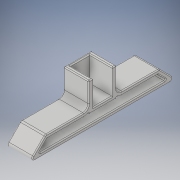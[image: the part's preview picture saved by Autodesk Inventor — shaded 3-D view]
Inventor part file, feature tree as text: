
AUTODESK INVENTOR PART (.ipt)
format: ipt  version: 2019 (Build 230136000, 136)  size: 265,728 bytes
history: native  units: in
note: dims shown in document units (in); Inventor stores cm internally (conversion verified against a paired STEP export)
features: fillet x4, sketch x3, extrude x2, mirror x1, shell x1
ambient origin geometry x8: Origin, YZ Plane, XZ Plane, XY Plane, X Axis, Y Axis, Z Axis, Center Point
bodies: Solid1 (feature_tree)
feature tree (11):
  sketch  "Sketch1"  dims[d0=2.2in d1=0.2933in d2=0.75in]
  extrude  "Extrusion1"  Depth=0.75in
  mirror  "Mirror1"
  shell  "Shell1"  Thickness=0.75in
  extrude  "Extrusion2"  Depth=0.5in
  fillet  "Fillet2"  Radius=0.1181in
  fillet  "Fillet3"  Radius=0.0787in
  fillet  "Fillet4"  Radius=0.1575in
  fillet  "Fillet5"  Radius=0.75in
  sketch  "Sketch2"  dims[d3=45.0deg d5=0.5in d6=0.1181in d7=0.0787in d8=0.1575in d9=0.75in d10=0.0in]
  sketch  "Sketch3"  dims[d12=0.1181in d13=0.0787in d14=0.0in d15=0.0276in d16=0.0276in d17=0.0276in d18=0.0276in]
